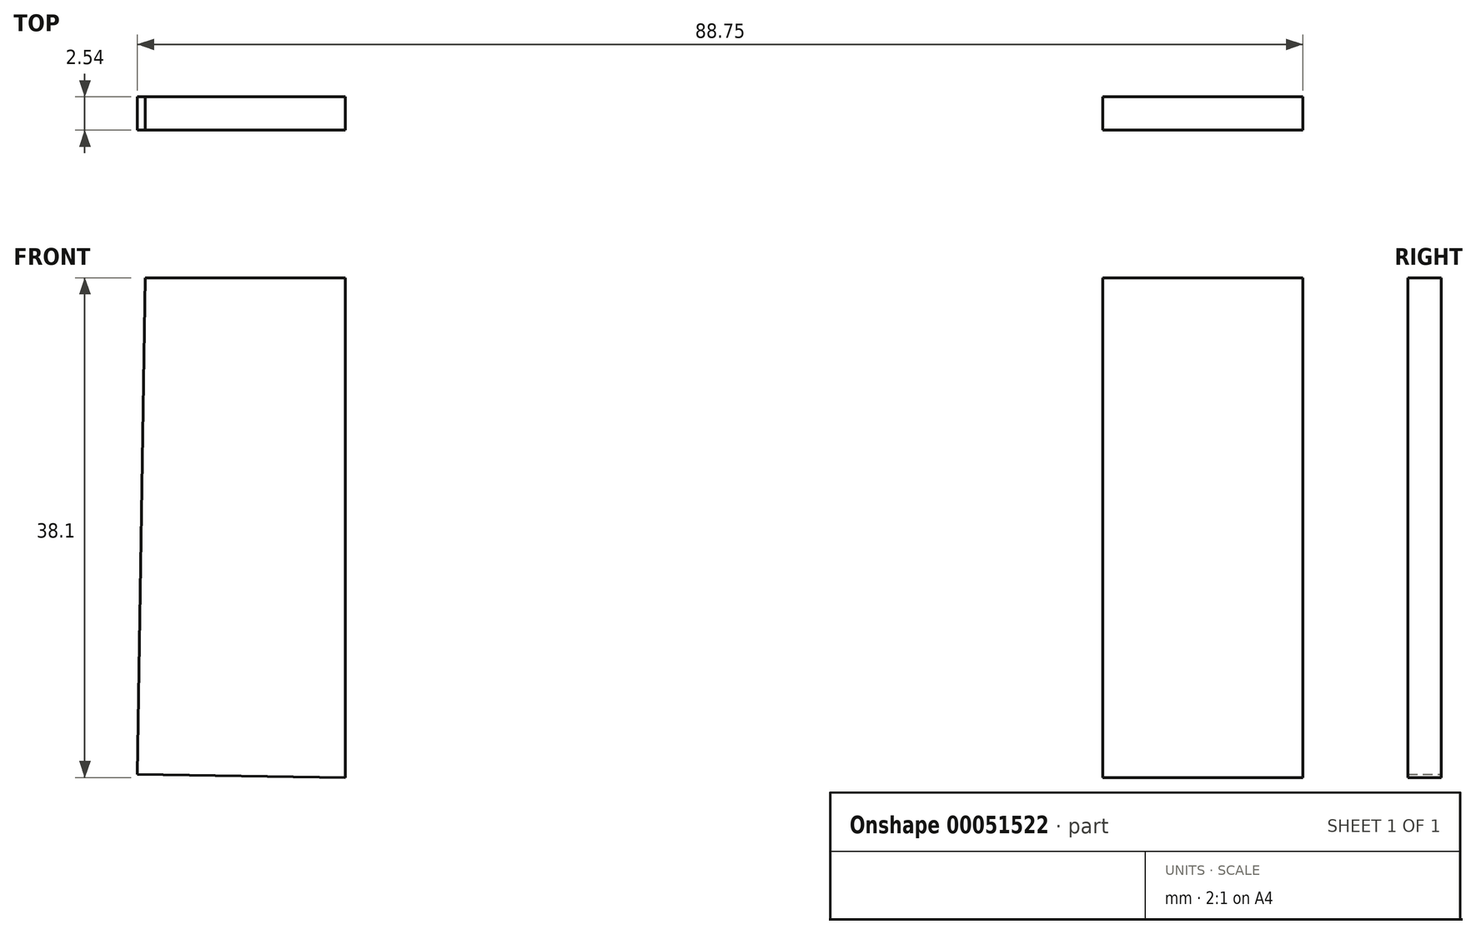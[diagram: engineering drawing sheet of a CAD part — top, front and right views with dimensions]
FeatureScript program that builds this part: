
annotation { "Feature Type Name" : "Feature", "Feature Type Description" : "" }
export const myFeature = defineFeature(function(context is Context, id is Id, definition is map)
    precondition{}
    {
        {
            var Q0;
            Q0=qCreatedBy(makeId("Front.planeOp"),FACE);
            var sketch = newSketch(context, id + "F0", { "sketchPlane" : qUnion([Q0])});
            skLineSegment(sketch, "E0", {"start": v(-50.53, 19.17) * mm, "end": v(-51.12, -18.68) * mm});
            skLineSegment(sketch, "E1", {"start": v(-51.12, -18.68) * mm, "end": v(-35.3, -18.93) * mm});
            skLineSegment(sketch, "E2", {"start": v(-35.3, -18.93) * mm, "end": v(-35.3, 19.17) * mm});
            skLineSegment(sketch, "E3", {"start": v(-35.3, 19.17) * mm, "end": v(-50.53, 19.17) * mm});
            skLineSegment(sketch, "E4", {"start": v(22.4, 19.17) * mm, "end": v(22.4, -18.93) * mm});
            skLineSegment(sketch, "E5", {"start": v(22.4, -18.93) * mm, "end": v(37.63, -18.93) * mm});
            skLineSegment(sketch, "E6", {"start": v(37.63, -18.93) * mm, "end": v(37.63, 19.17) * mm});
            skLineSegment(sketch, "E7", {"start": v(37.63, 19.17) * mm, "end": v(22.4, 19.17) * mm});
            skSolve(sketch);
        }
        {
            var Q0;
            Q0 = qSketchRegion(id + "F0", true);
            extrude(context, id + "F1", {"entities" : qUnion([Q0]), "depth" : 2.54 * mm});
        }
    });
